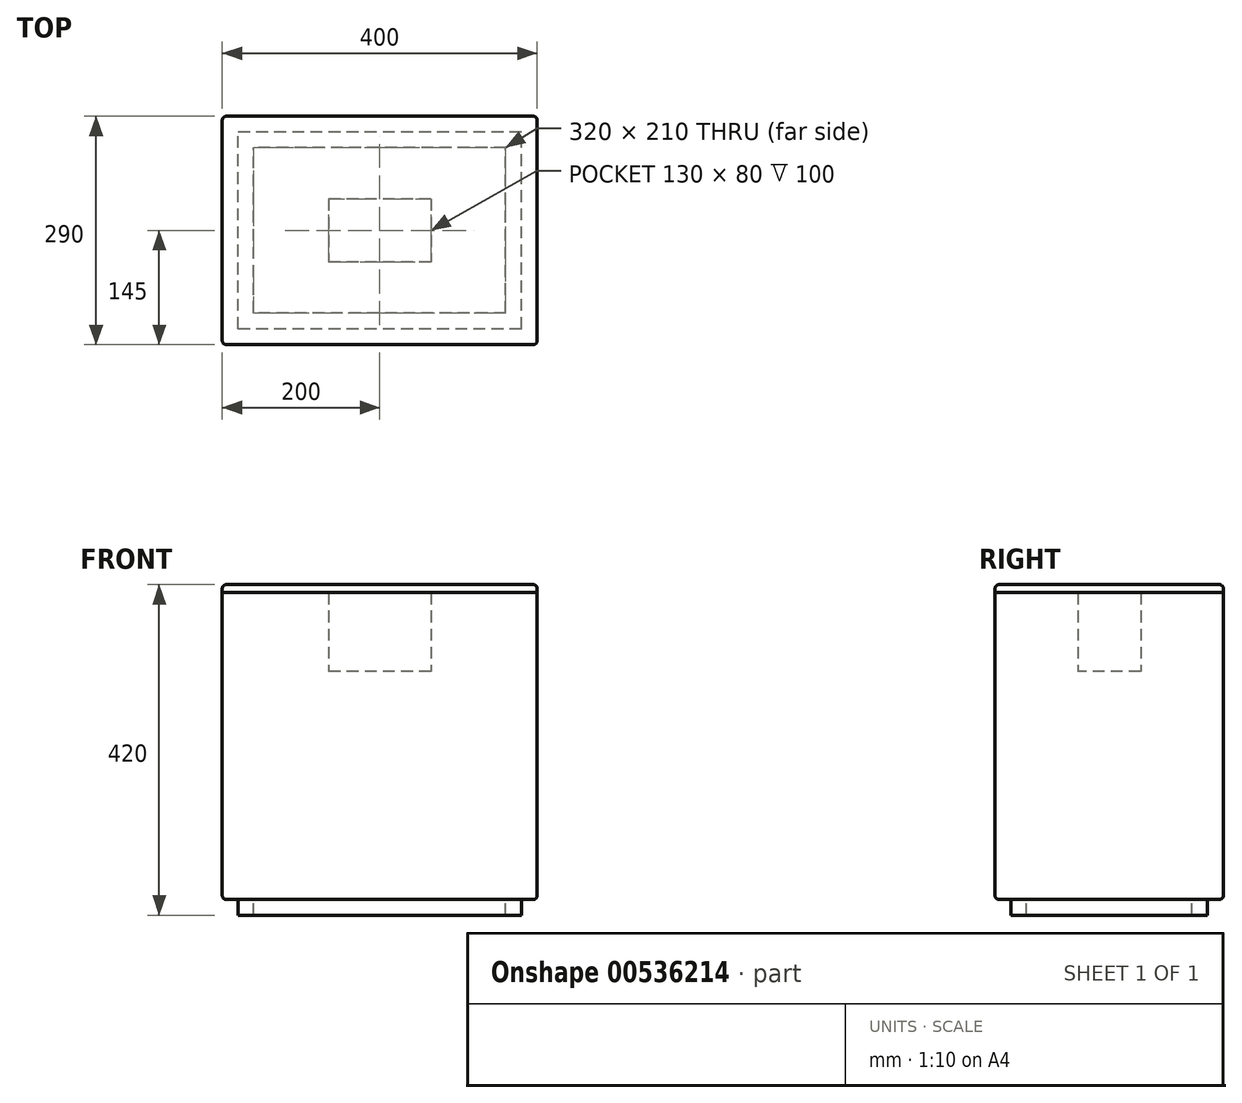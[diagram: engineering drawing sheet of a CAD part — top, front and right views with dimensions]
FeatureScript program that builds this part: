
annotation { "Feature Type Name" : "Feature", "Feature Type Description" : "" }
export const myFeature = defineFeature(function(context is Context, id is Id, definition is map)
    precondition{}
    {
        {
            var Q0;
            Q0=qCreatedBy(makeId("Top.planeOp"),FACE);
            var sketch = newSketch(context, id + "F0", { "sketchPlane" : qUnion([Q0])});
            skLineSegment(sketch, "E0.bottom", {"start": v(200, 145) * mm, "end": v(-200, 145) * mm});
            skLineSegment(sketch, "E0.top", {"start": v(200, -145) * mm, "end": v(-200, -145) * mm});
            skLineSegment(sketch, "E0.left", {"start": v(200, 145) * mm, "end": v(200, -145) * mm});
            skLineSegment(sketch, "E0.right", {"start": v(-200, 145) * mm, "end": v(-200, -145) * mm});
            skPoint(sketch, "E0.middle", {"position": v(0, 0) * mm});
            skSolve(sketch);
        }
        {
            var Q0;
            Q0=makeQuery(id+"F0.imprint","IMPRINT",FACE,{"disambiguationData":[TD([[makeQuery(id+"F0.imprint","IMPRINT",EDGE,{"derivedFrom":sQuery(id+"F0.wireOp",EDGE,"E0.bottom")}),1.0]])]});
            extrude(context, id + "F1", {"entities" : qUnion([Q0]), "depth" : 290 * mm, "offsetDistance" : 25.4 * mm});
        }
        {
            var Q0;
            Q0=makeQuery(id+"F1.opExtrude","CAP_FACE",FACE,{"disambiguationData":[OSD([sQuery(id+"F0.wireOp",EDGE,"E0.bottom"),sQuery(id+"F0.wireOp",EDGE,"E0.top"),sQuery(id+"F0.wireOp",EDGE,"E0.left"),sQuery(id+"F0.wireOp",EDGE,"E0.right")])],"isStart":false});
            var sketch = newSketch(context, id + "F2", { "sketchPlane" : qUnion([Q0])});
            skLineSegment(sketch, "E1.bottom", {"start": v(65, 40) * mm, "end": v(-65, 40) * mm});
            skLineSegment(sketch, "E1.top", {"start": v(65, -40) * mm, "end": v(-65, -40) * mm});
            skLineSegment(sketch, "E1.left", {"start": v(65, 40) * mm, "end": v(65, -40) * mm});
            skLineSegment(sketch, "E1.right", {"start": v(-65, 40) * mm, "end": v(-65, -40) * mm});
            skPoint(sketch, "E1.middle", {"position": v(0, 0) * mm});
            skSolve(sketch);
        }
        {
            var Q0;
            Q0=makeQuery(id+"F2.imprint","IMPRINT",FACE,{"disambiguationData":[TD([[makeQuery(id+"F2.imprint","IMPRINT",EDGE,{"derivedFrom":sQuery(id+"F2.wireOp",EDGE,"E1.bottom")}),-1.0]])]});
            extrude(context, id + "F3", {"entities" : qUnion([Q0]), "operationType" : NewBodyOperationType.ADD, "depth" : 100 * mm, "offsetDistance" : 25 * mm});
        }
        {
            var Q0;
            {var subQ0=sQuery(id+"F0.wireOp",EDGE,"E0.right");var subQ1=sQuery(id+"F0.wireOp",EDGE,"E0.top");Q0=makeQuery(id+"F3.boolean.opBoolean","MERGE",EDGE,{"derivedFrom":[makeQuery(id+"F1.opExtrude","SWEPT_EDGE",EDGE,{"disambiguationData":[OSD([subQ1,subQ0])]}),makeQuery(id+"F3.opExtrude","SWEPT_EDGE",EDGE,{"disambiguationData":[OSD([subQ1,subQ0])]})]});}
            var Q1;
            Q1=makeQuery(id+"F1.opExtrude","CAP_FACE",FACE,{"disambiguationData":[OSD([sQuery(id+"F0.wireOp",EDGE,"E0.bottom"),sQuery(id+"F0.wireOp",EDGE,"E0.top"),sQuery(id+"F0.wireOp",EDGE,"E0.left"),sQuery(id+"F0.wireOp",EDGE,"E0.right")])],"isStart":true});
            var Q2;
            {var subQ0=sQuery(id+"F0.wireOp",EDGE,"E0.right");var subQ1=sQuery(id+"F0.wireOp",EDGE,"E0.bottom");Q2=makeQuery(id+"F3.boolean.opBoolean","MERGE",EDGE,{"derivedFrom":[makeQuery(id+"F1.opExtrude","SWEPT_EDGE",EDGE,{"disambiguationData":[OSD([subQ1,subQ0])]}),makeQuery(id+"F3.opExtrude","SWEPT_EDGE",EDGE,{"disambiguationData":[OSD([subQ1,subQ0])]})]});}
            var Q3;
            {var subQ0=sQuery(id+"F0.wireOp",EDGE,"E0.left");var subQ1=sQuery(id+"F0.wireOp",EDGE,"E0.bottom");Q3=makeQuery(id+"F3.boolean.opBoolean","MERGE",EDGE,{"derivedFrom":[makeQuery(id+"F1.opExtrude","SWEPT_EDGE",EDGE,{"disambiguationData":[OSD([subQ1,subQ0])]}),makeQuery(id+"F3.opExtrude","SWEPT_EDGE",EDGE,{"disambiguationData":[OSD([subQ1,subQ0])]})]});}
            var Q4;
            {var subQ0=sQuery(id+"F0.wireOp",EDGE,"E0.left");var subQ1=sQuery(id+"F0.wireOp",EDGE,"E0.top");Q4=makeQuery(id+"F3.boolean.opBoolean","MERGE",EDGE,{"derivedFrom":[makeQuery(id+"F1.opExtrude","SWEPT_EDGE",EDGE,{"disambiguationData":[OSD([subQ1,subQ0])]}),makeQuery(id+"F3.opExtrude","SWEPT_EDGE",EDGE,{"disambiguationData":[OSD([subQ1,subQ0])]})]});}
            fillet(context, id + "F4", {"entities" : qUnion([Q0, Q1, Q2, Q3, Q4]), "radius" : 5 * mm, "tangentPropagation" : true, "allowEdgeOverflow" : false});
        }
        {
            var Q0;
            Q0=makeQuery(id+"F1.opExtrude","CAP_FACE",FACE,{"disambiguationData":[OSD([sQuery(id+"F0.wireOp",EDGE,"E0.bottom"),sQuery(id+"F0.wireOp",EDGE,"E0.top"),sQuery(id+"F0.wireOp",EDGE,"E0.left"),sQuery(id+"F0.wireOp",EDGE,"E0.right")])],"isStart":true});
            var sketch = newSketch(context, id + "F5", { "sketchPlane" : qUnion([Q0])});
            skLineSegment(sketch, "E2.bottom", {"start": v(180, 125) * mm, "end": v(-180, 125) * mm});
            skLineSegment(sketch, "E2.top", {"start": v(180, -125) * mm, "end": v(-180, -125) * mm});
            skLineSegment(sketch, "E2.left", {"start": v(180, 125) * mm, "end": v(180, -125) * mm});
            skLineSegment(sketch, "E2.right", {"start": v(-180, 125) * mm, "end": v(-180, -125) * mm});
            skPoint(sketch, "E2.middle", {"position": v(0, 0) * mm});
            skLineSegment(sketch, "E3.bottom", {"start": v(160, 105) * mm, "end": v(-160, 105) * mm});
            skLineSegment(sketch, "E3.top", {"start": v(160, -105) * mm, "end": v(-160, -105) * mm});
            skLineSegment(sketch, "E3.left", {"start": v(160, 105) * mm, "end": v(160, -105) * mm});
            skLineSegment(sketch, "E3.right", {"start": v(-160, 105) * mm, "end": v(-160, -105) * mm});
            skSolve(sketch);
        }
        {
            var Q0;
            Q0 = qSketchRegion(id + "F5", true);
            extrude(context, id + "F6", {"entities" : qUnion([Q0]), "depth" : 20 * mm, "offsetDistance" : 25 * mm});
        }
        {
            var Q0;
            Q0=makeQuery(id+"F3.opExtrude","CAP_FACE",FACE,{"disambiguationData":[OSD([sQuery(id+"F0.wireOp",EDGE,"E0.bottom"),sQuery(id+"F0.wireOp",EDGE,"E0.top"),sQuery(id+"F0.wireOp",EDGE,"E0.left"),sQuery(id+"F0.wireOp",EDGE,"E0.right"),sQuery(id+"F2.wireOp",EDGE,"E1.bottom"),sQuery(id+"F2.wireOp",EDGE,"E1.top"),sQuery(id+"F2.wireOp",EDGE,"E1.left"),sQuery(id+"F2.wireOp",EDGE,"E1.right")])],"isStart":false});
            var sketch = newSketch(context, id + "F7", { "sketchPlane" : qUnion([Q0])});
            skSolve(sketch);
        }
        {
            var Q0;
            Q0 = qSketchRegion(id + "F7", true);
            var Q1;
            Q1=makeQuery(id+"F7.imprint","IMPRINT",FACE,{"disambiguationData":[TD([[makeQuery(id+"F7.imprint","IMPRINT",EDGE,{"derivedFrom":makeQuery(id+"F3.opExtrude","CAP_EDGE",EDGE,{"disambiguationData":[OSD([sQuery(id+"F2.wireOp",EDGE,"E1.bottom")])],"isStart":false})}),1.0]])]});
            var Q2;
            {var subQ3=sQuery(id+"F2.wireOp",EDGE,"E1.bottom");Q2=makeQuery(id+"F7.imprint","IMPRINT",FACE,{"disambiguationData":[TD([[makeQuery(id+"F7.imprint","IMPRINT",EDGE,{"derivedFrom":makeQuery(id+"F3.opExtrude","CAP_EDGE",EDGE,{"disambiguationData":[OSD([subQ3])],"isStart":false})}),-1.0]])]});}
            extrude(context, id + "F8", {"entities" : qUnion([Q0, Q1, Q2]), "depth" : 10 * mm, "offsetDistance" : 25 * mm});
        }
        {
            var Q0;
            Q0=makeQuery(id+"F8.opExtrude","CAP_EDGE",EDGE,{"disambiguationData":[OSD([sQuery(id+"F0.wireOp",EDGE,"E0.right")])],"isStart":false});
            var Q1;
            Q1=makeQuery(id+"F8.opExtrude","CAP_EDGE",EDGE,{"disambiguationData":[OSD([sQuery(id+"F0.wireOp",EDGE,"E0.bottom")])],"isStart":false});
            fillet(context, id + "F9", {"entities" : qUnion([Q0, Q1]), "radius" : 5 * mm, "tangentPropagation" : true, "allowEdgeOverflow" : false});
        }
    });
